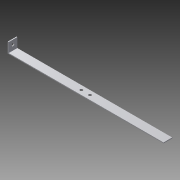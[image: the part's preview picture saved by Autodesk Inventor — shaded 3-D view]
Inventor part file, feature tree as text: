
AUTODESK INVENTOR PART (.ipt)
format: ipt  version: 2015 (Build 190159000, 159)  size: 115,200 bytes
history: native  units: mm
features: sketch x4, extrude x2, hole x2, other x1
ambient origin geometry x8: Origin, YZ Plane, XZ Plane, XY Plane, X Axis, Y Axis, Z Axis, Center Point
bodies: Body1 (feature_tree)
feature tree (9):
  other  "ソリッド1"
  extrude  "押し出し1"  Depth=10.0mm
  hole  "穴2"  [1 undecoded]
  extrude  "押し出し2"  Depth=1.0mm TaperAngle=0.0deg
  hole  "穴3"  [1 undecoded]
  sketch  "スケッチ1"
  sketch  "スケッチ3"
  sketch  "スケッチ4"
  sketch  "スケッチ5"
note: 2 required parameter values undecoded (feature->parameter linkage not recoverable at this tier; creation-order binding heuristic only, values carry confidence <= 0.55)
